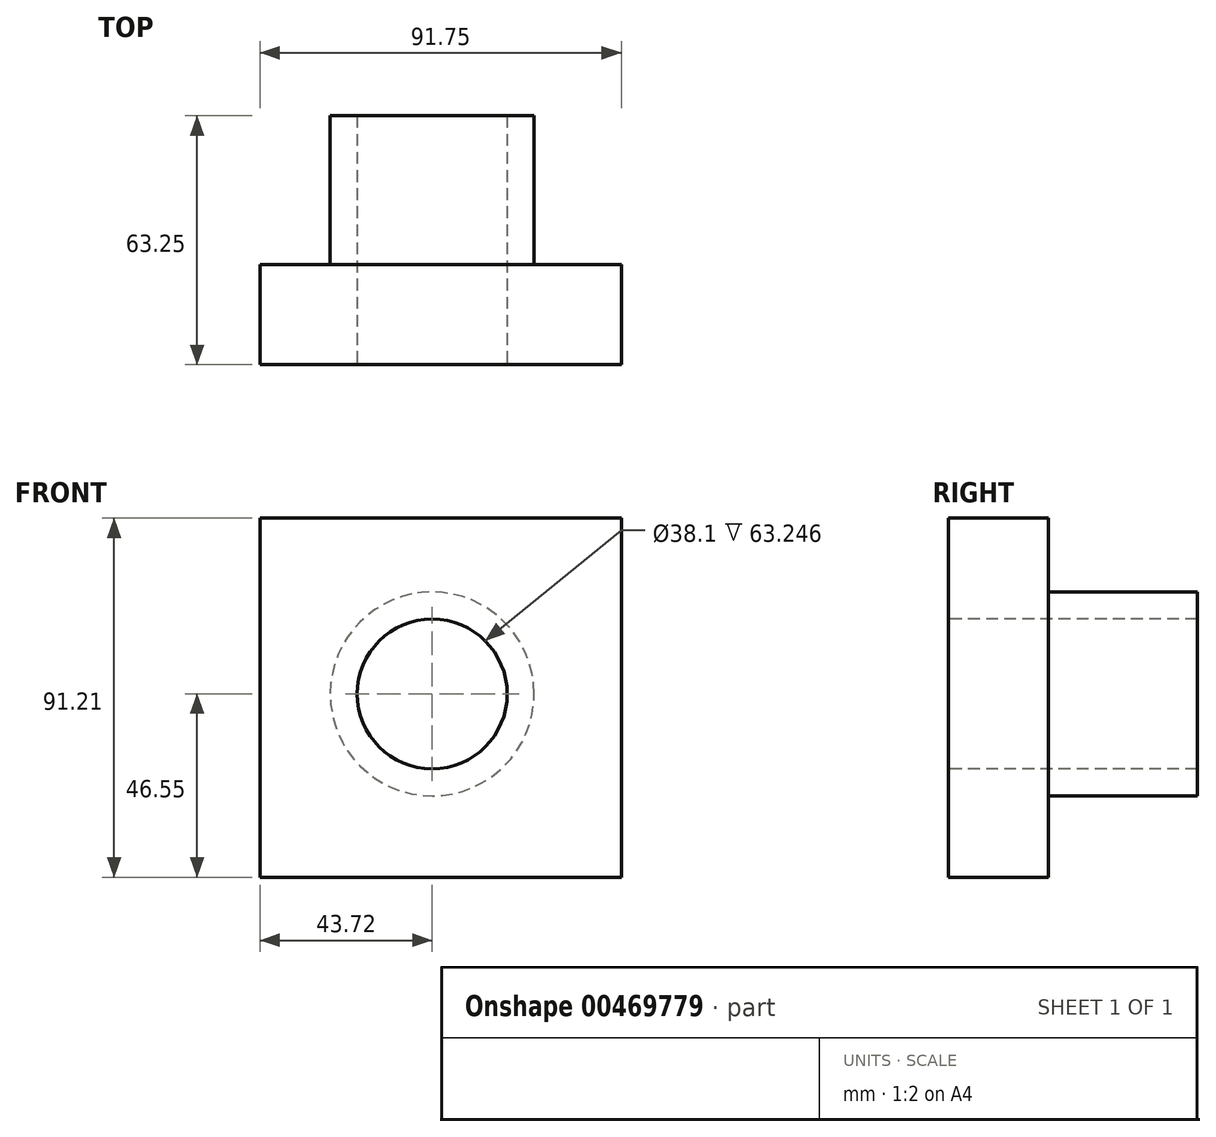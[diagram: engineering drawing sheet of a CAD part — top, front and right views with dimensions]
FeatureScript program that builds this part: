
annotation { "Feature Type Name" : "Feature", "Feature Type Description" : "" }
export const myFeature = defineFeature(function(context is Context, id is Id, definition is map)
    precondition{}
    {
        {
            var Q0;
            Q0=qCreatedBy(makeId("Front.planeOp"),FACE);
            var sketch = newSketch(context, id + "F0", { "sketchPlane" : qUnion([Q0])});
            skLineSegment(sketch, "E0.bottom", {"start": v(-43.72, 44.66) * mm, "end": v(48.03, 44.66) * mm});
            skLineSegment(sketch, "E0.top", {"start": v(-43.72, -46.55) * mm, "end": v(48.03, -46.55) * mm});
            skLineSegment(sketch, "E0.left", {"start": v(-43.72, 44.66) * mm, "end": v(-43.72, -46.55) * mm});
            skLineSegment(sketch, "E0.right", {"start": v(48.03, 44.66) * mm, "end": v(48.03, -46.55) * mm});
            skSolve(sketch);
        }
        {
            var Q0;
            Q0=makeQuery(id+"F0.imprint","IMPRINT",FACE,{"disambiguationData":[TD([[makeQuery(id+"F0.imprint","IMPRINT",EDGE,{"derivedFrom":sQuery(id+"F0.wireOp",EDGE,"E0.bottom")}),-1.0]])]});
            extrude(context, id + "F1", {"entities" : qUnion([Q0]), "depth" : 25.4 * mm});
        }
        {
            var Q0;
            Q0=makeQuery(id+"F1.opExtrude","CAP_FACE",FACE,{"disambiguationData":[OSD([sQuery(id+"F0.wireOp",EDGE,"E0.bottom"),sQuery(id+"F0.wireOp",EDGE,"E0.top"),sQuery(id+"F0.wireOp",EDGE,"E0.left"),sQuery(id+"F0.wireOp",EDGE,"E0.right")])],"isStart":false});
            var sketch = newSketch(context, id + "F2", { "sketchPlane" : qUnion([Q0])});
            skCircle(sketch, "E1", {"center": v(0, 0) * mm, "radius": 25.9 * mm});
            skSolve(sketch);
        }
        {
            var Q0;
            Q0=makeQuery(id+"F2.imprint","IMPRINT",FACE,{"disambiguationData":[TD([[makeQuery(id+"F2.imprint","IMPRINT",EDGE,{"derivedFrom":sQuery(id+"F2.wireOp",EDGE,"E1")}),1.0]])]});
            var sketch = newSketch(context, id + "F3", { "sketchPlane" : qUnion([Q0])});
            skCircle(sketch, "E2", {"center": v(0, 0) * mm, "radius": 31.51 * mm});
            skSolve(sketch);
        }
        {
            var Q0;
            Q0=sQuery(id+"F3.wireOp",VERTEX,"E2.center");
            var Q1;
            Q1=makeQuery(id+"F1.opExtrude","SWEPT_BODY",BODY,{"disambiguationData":[OSD([sQuery(id+"F0.wireOp",EDGE,"E0.bottom"),sQuery(id+"F0.wireOp",EDGE,"E0.top"),sQuery(id+"F0.wireOp",EDGE,"E0.left"),sQuery(id+"F0.wireOp",EDGE,"E0.right")])]});
            hole(context, id + "F4", {"style" : HoleStyle.SIMPLE, "endStyle" : HoleEndStyle.THROUGH, "holeDiameter" : 50.8 * mm, "isTappedThrough" : true, "tappedDepth" : 12.7 * mm, "tapClearance" : 3, "locations" : qUnion([Q0]), "scope" : qUnion([Q1])});
        }
        {
            var Q0;
            Q0=makeQuery(id+"F2.imprint","IMPRINT",FACE,{"disambiguationData":[TD([[makeQuery(id+"F2.imprint","IMPRINT",EDGE,{"derivedFrom":sQuery(id+"F2.wireOp",EDGE,"E1")}),1.0]])]});
            var sketch = newSketch(context, id + "F5", { "sketchPlane" : qUnion([Q0])});
            skCircle(sketch, "E3", {"center": v(0, 0) * mm, "radius": 31.97 * mm});
            skSolve(sketch);
        }
        {
            var Q0;
            Q0=makeQuery(id+"F2.imprint","IMPRINT",FACE,{"disambiguationData":[TD([[makeQuery(id+"F2.imprint","IMPRINT",EDGE,{"derivedFrom":sQuery(id+"F2.wireOp",EDGE,"E1")}),1.0]])]});
            extrude(context, id + "F6", {"entities" : qUnion([Q0]), "operationType" : NewBodyOperationType.ADD, "oppositeDirection" : true, "depth" : 63.25 * mm});
        }
        {
            var Q0;
            Q0=sQuery(id+"F5.wireOp",VERTEX,"E3.center");
            var Q1;
            Q1=makeQuery(id+"F1.opExtrude","SWEPT_BODY",BODY,{"disambiguationData":[OSD([sQuery(id+"F0.wireOp",EDGE,"E0.bottom"),sQuery(id+"F0.wireOp",EDGE,"E0.top"),sQuery(id+"F0.wireOp",EDGE,"E0.left"),sQuery(id+"F0.wireOp",EDGE,"E0.right")])]});
            hole(context, id + "F7", {"style" : HoleStyle.SIMPLE, "endStyle" : HoleEndStyle.THROUGH, "holeDiameter" : 38.1 * mm, "isTappedThrough" : true, "tappedDepth" : 12.7 * mm, "tapClearance" : 3, "locations" : qUnion([Q0]), "scope" : qUnion([Q1])});
        }
    });
